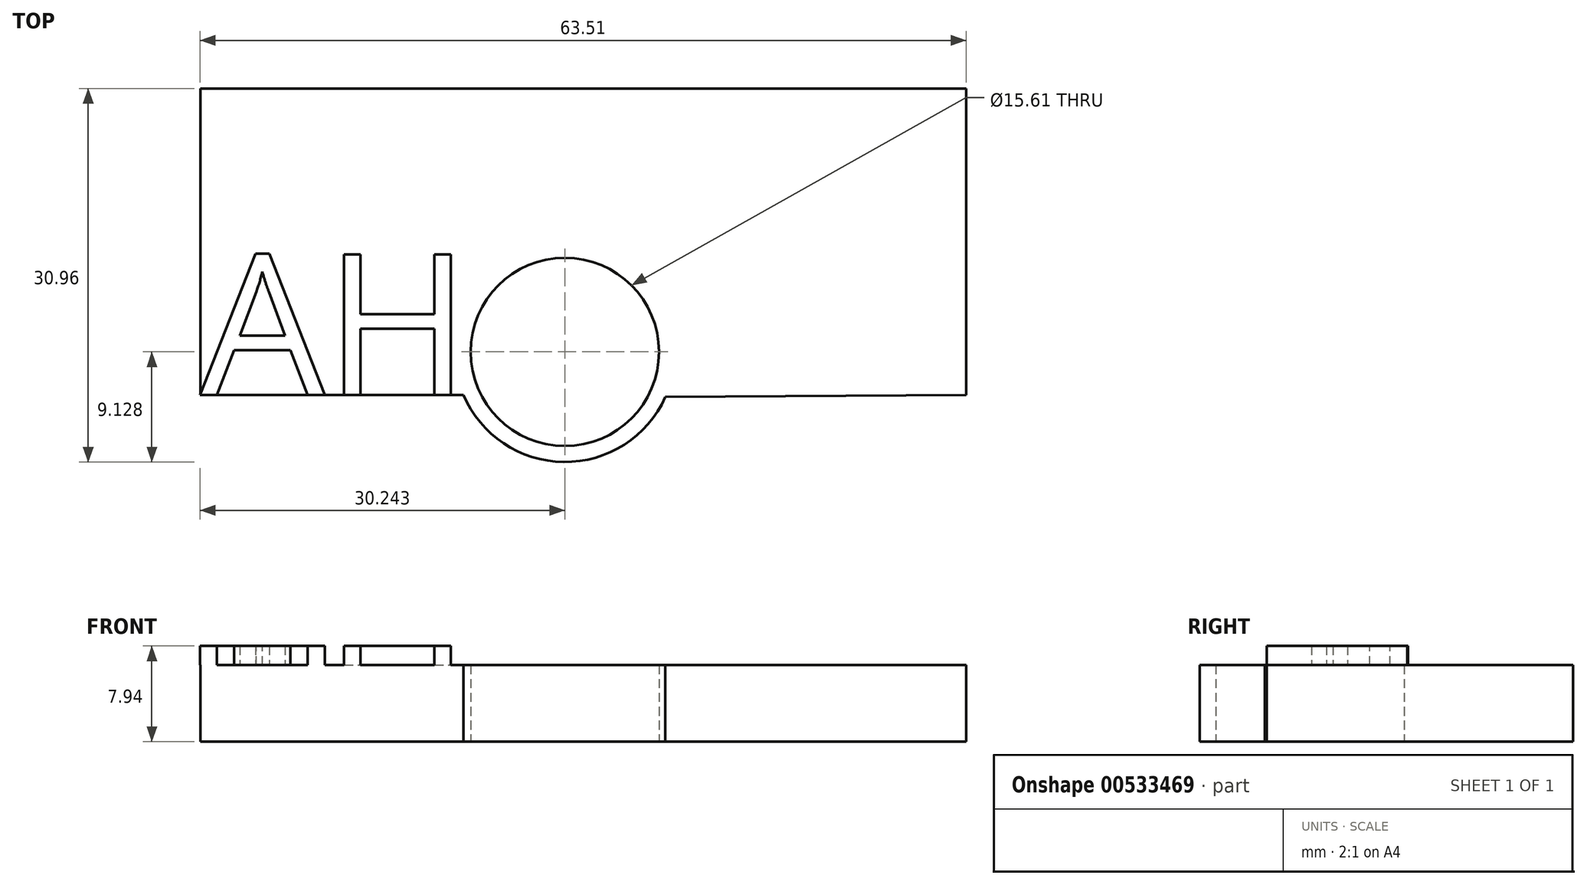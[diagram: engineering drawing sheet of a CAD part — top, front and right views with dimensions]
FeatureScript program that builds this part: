
annotation { "Feature Type Name" : "Feature", "Feature Type Description" : "" }
export const myFeature = defineFeature(function(context is Context, id is Id, definition is map)
    precondition{}
    {
        {
            var Q0;
            Q0=qCreatedBy(makeId("Top.planeOp"),FACE);
            var sketch = newSketch(context, id + "F0", { "sketchPlane" : qUnion([Q0])});
            skLineSegment(sketch, "E0", {"start": v(-49.6, 38.9) * mm, "end": v(13.9, 38.9) * mm});
            skLineSegment(sketch, "E1", {"start": v(13.9, 38.9) * mm, "end": v(13.9, 13.5) * mm});
            skLineSegment(sketch, "E2", {"start": v(-49.6, 13.5) * mm, "end": v(-49.6, 38.9) * mm});
            skPoint(sketch, "E3.centerSnap0", {"position": v(-49.6, 26.2) * mm});
            skCircle(sketch, "E4", {"center": v(-19.36, 17.07) * mm, "radius": 9.13 * mm});
            skLineSegment(sketch, "E5", {"start": v(-49.6, 13.5) * mm, "end": v(-27.76, 13.5) * mm});
            skLineSegment(sketch, "E6", {"start": v(-11.03, 13.32) * mm, "end": v(13.9, 13.5) * mm});
            skCircle(sketch, "E7", {"center": v(-19.36, 17.07) * mm, "radius": 7.8 * mm});
            skSolve(sketch);
        }
        {
            var Q0;
            Q0 = qSketchRegion(id + "F0", true);
            extrude(context, id + "F1", {"entities" : qUnion([Q0]), "depth" : 6.35 * mm, "offsetDistance" : 25.4 * mm});
        }
        {
            var Q0;
            Q0=makeQuery(id+"F1.opExtrude","CAP_FACE",FACE,{"disambiguationData":[OSD([sQuery(id+"F0.wireOp",EDGE,"E0"),sQuery(id+"F0.wireOp",EDGE,"E1"),sQuery(id+"F0.wireOp",EDGE,"E2"),sQuery(id+"F0.wireOp",EDGE,"E4"),sQuery(id+"F0.wireOp",EDGE,"E5"),sQuery(id+"F0.wireOp",EDGE,"E6"),sQuery(id+"F0.wireOp",EDGE,"E7")])],"isStart":false});
            var sketch = newSketch(context, id + "F2", { "sketchPlane" : qUnion([Q0])});
            skText(sketch, "E8", { "text": "AH\n", "fontName": "OpenSans-Regular.ttf"});
            const initialGuessF2  = {"E8": [-0.0496, 0.0135, 1, 0, 0.01175]};
            skSetInitialGuess(sketch, initialGuessF2);
            skSolve(sketch);
        }
        {
            var Q0;
            Q0 = qSketchRegion(id + "F2", true);
            extrude(context, id + "F3", {"entities" : qUnion([Q0]), "operationType" : NewBodyOperationType.ADD, "depth" : 1.59 * mm, "offsetDistance" : 25.4 * mm});
        }
    });
